# Revit family: Bath-Freestanding-KOHLER-Artifacts-K-21000_1
name_source: partatom
category: Plumbing Fixtures
revit_build: Autodesk Revit 2015 (Build: 20140606_1530(x64)
units: mm (PartAtom-declared; Revit-internal decimal feet)

## types (1)
- not a Type-See Type Catalog
    ADA Compliant = No
    Assembly Code = D2010500
    Bath Base = No
    Bath Base Included = No
    Bath Base Material = <By Category>
    CW Connection = No
    Cold Water Inlet = Cold Water Inlet
    Date Modified = 07/25/2019
    Decorative Border = No
    Default Elevation = 0"
    Description = 66 inch x 33 inch freestanding bath with Biscuit exterior
    Drain Included = No
    Finish = Default
    HW Connection = No
    Height = 27 7/8"
    Height1 = 15/16"
    Hot Water Inlet = Hot Water Inlet
    Legs = Yes
    Legs Included = No
    Legs Material = Default
    Length = 66 1/8"
    Manufacturer = KOHLER Co.
    MasterFormat 1995 = 15410
    MasterFormat 2004 = 22.41.19
    Material = Enameled Cast Iron
    Model = K-21000-B-96
    Outerside Material = Default
    Product Documentation Link = https://www.us.kohler.com
    Product Name = Artifacts
    Product Page URL = http://www.us.kohler.com
    Type = 1
    URL = https://www.us.kohler.com
    Vent Connection = No
    Waste Connection = Yes
    Waste Water Outlet = Waste Water Outlet
    WaterSense Certified = No
    Width = 32 1/2"

## geometry (parser evidence)
native form markers: Sweep x8
no freeform markers — native parametric forms only
